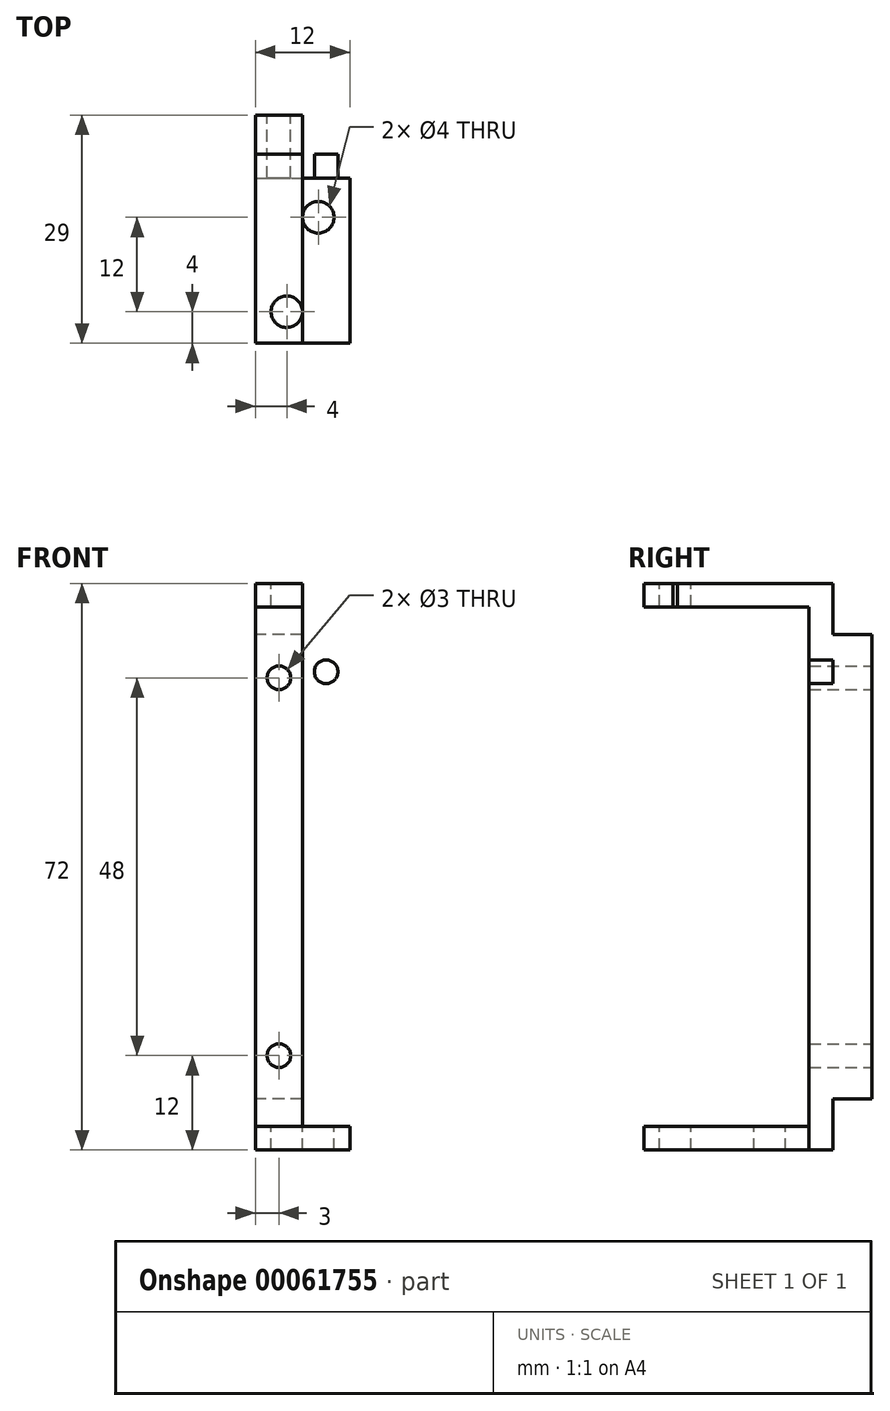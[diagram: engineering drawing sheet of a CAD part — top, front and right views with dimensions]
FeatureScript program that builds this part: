
annotation { "Feature Type Name" : "Feature", "Feature Type Description" : "" }
export const myFeature = defineFeature(function(context is Context, id is Id, definition is map)
    precondition{}
    {
        {
            var Q0;
            Q0=qCreatedBy(makeId("Right.planeOp"),FACE);
            var sketch = newSketch(context, id + "F0", { "sketchPlane" : qUnion([Q0])});
            skLineSegment(sketch, "E0", {"start": v(-10.5, 37.5) * mm, "end": v(18.5, 37.5) * mm});
            skLineSegment(sketch, "E1", {"start": v(18.5, 37.5) * mm, "end": v(18.5, -34.5) * mm});
            skLineSegment(sketch, "E2.0", {"start": v(10.5, 34.5) * mm, "end": v(10.5, -34.5) * mm});
            skLineSegment(sketch, "E2.1", {"start": v(-10.5, 34.5) * mm, "end": v(10.5, 34.5) * mm});
            skLineSegment(sketch, "E3", {"start": v(-10.5, 37.5) * mm, "end": v(-10.5, 34.5) * mm});
            skLineSegment(sketch, "E4", {"start": v(18.5, -34.5) * mm, "end": v(10.5, -34.5) * mm});
            skLineSegment(sketch, "E5", {"start": v(10.5, 0) * mm, "end": v(-14.36, 0) * mm, "construction": true});
            skLineSegment(sketch, "E6", {"start": v(0, 34.5) * mm, "end": v(0, -1.72) * mm, "construction": true});
            skSolve(sketch);
        }
        {
            var Q0;
            Q0=makeQuery(id+"F0.imprint","IMPRINT",FACE,{"disambiguationData":[TD([[makeQuery(id+"F0.imprint","IMPRINT",EDGE,{"derivedFrom":sQuery(id+"F0.wireOp",EDGE,"E0")}),-1.0]])]});
            extrude(context, id + "F1", {"entities" : qUnion([Q0]), "depth" : 12 * mm});
        }
        {
            var Q0;
            Q0=makeQuery(id+"F1.opExtrude","SWEPT_FACE",FACE,{"disambiguationData":[OSD([sQuery(id+"F0.wireOp",EDGE,"E0")])]});
            var sketch = newSketch(context, id + "F2", { "sketchPlane" : qUnion([Q0])});
            skLineSegment(sketch, "E7.bottom", {"start": v(0, 18.5) * mm, "end": v(6.02, 18.5) * mm});
            skLineSegment(sketch, "E7.top", {"start": v(0, 13.5) * mm, "end": v(6.02, 13.5) * mm});
            skLineSegment(sketch, "E7.left", {"start": v(0, 18.5) * mm, "end": v(0, 13.5) * mm});
            skLineSegment(sketch, "E7.right", {"start": v(6.02, 18.5) * mm, "end": v(6.02, 13.5) * mm});
            skSolve(sketch);
        }
        {
            var Q0;
            Q0=makeQuery(id+"F2.imprint","IMPRINT",FACE,{"disambiguationData":[TD([[makeQuery(id+"F2.imprint","IMPRINT",EDGE,{"derivedFrom":sQuery(id+"F2.wireOp",EDGE,"E7.bottom")}),1.0]])]});
            extrude(context, id + "F3", {"entities" : qUnion([Q0]), "operationType" : NewBodyOperationType.REMOVE, "oppositeDirection" : true, "depth" : 72 * mm});
        }
        {
            var Q0;
            Q0=makeQuery(id+"F1.opExtrude","SWEPT_FACE",FACE,{"disambiguationData":[OSD([sQuery(id+"F0.wireOp",EDGE,"E1")])]});
            var sketch = newSketch(context, id + "F4", { "sketchPlane" : qUnion([Q0])});
            skCircle(sketch, "E8", {"center": v(-9, 25.5) * mm, "radius": 1.5 * mm});
            skCircle(sketch, "E9", {"center": v(-9, -22.5) * mm, "radius": 1.5 * mm});
            skLineSegment(sketch, "E10", {"start": v(-9, 25.5) * mm, "end": v(-9, -22.5) * mm, "construction": true});
            skPoint(sketch, "E11", {"position": v(-9, 37.5) * mm});
            skLineSegment(sketch, "E12", {"start": v(-9, 25.5) * mm, "end": v(-9, 37.5) * mm, "construction": true});
            skSolve(sketch);
        }
        {
            var Q0;
            Q0=makeQuery(id+"F4.imprint","IMPRINT",FACE,{"disambiguationData":[TD([[makeQuery(id+"F4.imprint","IMPRINT",EDGE,{"derivedFrom":sQuery(id+"F4.wireOp",EDGE,"E8")}),1.0]])]});
            var Q1;
            Q1=makeQuery(id+"F4.imprint","IMPRINT",FACE,{"disambiguationData":[TD([[makeQuery(id+"F4.imprint","IMPRINT",EDGE,{"derivedFrom":sQuery(id+"F4.wireOp",EDGE,"E9")}),1.0]])]});
            extrude(context, id + "F5", {"entities" : qUnion([Q0, Q1]), "operationType" : NewBodyOperationType.REMOVE, "oppositeDirection" : true, "depth" : 25 * mm});
        }
        {
            var Q0;
            Q0=makeQuery(id+"F3.boolean.opBoolean","COPY",FACE,{"derivedFrom":makeQuery(id+"F3.opExtrude","SWEPT_FACE",FACE,{"disambiguationData":[OSD([sQuery(id+"F2.wireOp",EDGE,"E7.top")])]})});
            var sketch = newSketch(context, id + "F6", { "sketchPlane" : qUnion([Q0])});
            skCircle(sketch, "E13.0", {"center": v(-3, 26.27) * mm, "radius": 1.5 * mm});
            skCircle(sketch, "E14.0", {"center": v(-3, -23.27) * mm, "radius": 1.5 * mm});
            skLineSegment(sketch, "E15", {"start": v(-3, 37.5) * mm, "end": v(-3, 26.27) * mm, "construction": true});
            skLineSegment(sketch, "E16", {"start": v(-3, 26.27) * mm, "end": v(-3, -23.27) * mm, "construction": true});
            skSolve(sketch);
        }
        {
            var Q0;
            Q0=makeQuery(id+"F6.imprint","IMPRINT",FACE,{"disambiguationData":[TD([[makeQuery(id+"F6.imprint","IMPRINT",EDGE,{"derivedFrom":sQuery(id+"F6.wireOp",EDGE,"E14.0")}),1.0]])]});
            var Q1;
            Q1=makeQuery(id+"F6.imprint","IMPRINT",FACE,{"disambiguationData":[TD([[makeQuery(id+"F6.imprint","IMPRINT",EDGE,{"derivedFrom":sQuery(id+"F6.wireOp",EDGE,"E13.0")}),-1.0]])]});
            extrude(context, id + "F7", {"entities" : qUnion([Q0, Q1]), "operationType" : NewBodyOperationType.REMOVE, "oppositeDirection" : true, "depth" : 25 * mm});
        }
        {
            var Q0;
            Q0=makeQuery(id+"F1.opExtrude","SWEPT_FACE",FACE,{"disambiguationData":[OSD([sQuery(id+"F0.wireOp",EDGE,"E2.0")])]});
            var sketch = newSketch(context, id + "F8", { "sketchPlane" : qUnion([Q0])});
            skLineSegment(sketch, "E17.bottom", {"start": v(12, -34.5) * mm, "end": v(0, -34.5) * mm});
            skLineSegment(sketch, "E17.top", {"start": v(12, -31.5) * mm, "end": v(0, -31.5) * mm});
            skLineSegment(sketch, "E17.left", {"start": v(12, -34.5) * mm, "end": v(12, -31.5) * mm});
            skLineSegment(sketch, "E17.right", {"start": v(0, -34.5) * mm, "end": v(0, -31.5) * mm});
            skSolve(sketch);
        }
        {
            var Q0;
            Q0=makeQuery(id+"F8.imprint","IMPRINT",FACE,{"disambiguationData":[TD([[makeQuery(id+"F8.imprint","IMPRINT",EDGE,{"derivedFrom":sQuery(id+"F8.wireOp",EDGE,"E17.bottom")}),-1.0]])]});
            extrude(context, id + "F9", {"entities" : qUnion([Q0]), "operationType" : NewBodyOperationType.ADD, "depth" : 21 * mm});
        }
        {
            var Q0;
            Q0=makeQuery(id+"F1.opExtrude","SWEPT_FACE",FACE,{"disambiguationData":[OSD([sQuery(id+"F0.wireOp",EDGE,"E0")])]});
            var sketch = newSketch(context, id + "F10", { "sketchPlane" : qUnion([Q0])});
            skCircle(sketch, "E18", {"center": v(4, 5.5) * mm, "radius": 2 * mm});
            skCircle(sketch, "E19", {"center": v(8, -6.5) * mm, "radius": 2 * mm});
            skSolve(sketch);
        }
        {
            var Q0;
            Q0=makeQuery(id+"F10.imprint","IMPRINT",FACE,{"disambiguationData":[TD([[makeQuery(id+"F10.imprint","IMPRINT",EDGE,{"derivedFrom":sQuery(id+"F10.wireOp",EDGE,"E18")}),1.0]])]});
            var Q1;
            Q1=makeQuery(id+"F10.imprint","IMPRINT",FACE,{"disambiguationData":[TD([[makeQuery(id+"F10.imprint","IMPRINT",EDGE,{"derivedFrom":sQuery(id+"F10.wireOp",EDGE,"E19")}),1.0]])]});
            extrude(context, id + "F11", {"entities" : qUnion([Q0, Q1]), "operationType" : NewBodyOperationType.REMOVE, "oppositeDirection" : true, "depth" : 72 * mm});
        }
        {
            var Q0;
            Q0=makeQuery(id+"F1.opExtrude","SWEPT_BODY",BODY,{"disambiguationData":[OSD([sQuery(id+"F0.wireOp",EDGE,"E0"),sQuery(id+"F0.wireOp",EDGE,"E1"),sQuery(id+"F0.wireOp",EDGE,"E2.0"),sQuery(id+"F0.wireOp",EDGE,"E2.1"),sQuery(id+"F0.wireOp",EDGE,"E3"),sQuery(id+"F0.wireOp",EDGE,"E4")])]});
            var Q1;
            Q1=makeQuery(id+"F1.opExtrude","CAP_FACE",FACE,{"disambiguationData":[OSD([sQuery(id+"F0.wireOp",EDGE,"E0"),sQuery(id+"F0.wireOp",EDGE,"E1"),sQuery(id+"F0.wireOp",EDGE,"E2.0"),sQuery(id+"F0.wireOp",EDGE,"E2.1"),sQuery(id+"F0.wireOp",EDGE,"E3"),sQuery(id+"F0.wireOp",EDGE,"E4")])],"isStart":false});
            mirror(context, id + "F12", {"entities" : qUnion([Q0]), "mirrorPlane" : qUnion([Q1])});
        }
        {
            var Q0;
            Q0=makeQuery(id+"F1.opExtrude","SWEPT_BODY",BODY,{"disambiguationData":[OSD([sQuery(id+"F0.wireOp",EDGE,"E0"),sQuery(id+"F0.wireOp",EDGE,"E1"),sQuery(id+"F0.wireOp",EDGE,"E2.0"),sQuery(id+"F0.wireOp",EDGE,"E2.1"),sQuery(id+"F0.wireOp",EDGE,"E3"),sQuery(id+"F0.wireOp",EDGE,"E4")])]});
            deleteBodies(context, id + "F13", {"entities" : qUnion([Q0])});
        }
        {
            var Q0;
            Q0=makeQuery(id+"F12.opPattern","COPY",FACE,{"derivedFrom":makeQuery(id+"F1.opExtrude","SWEPT_FACE",FACE,{"disambiguationData":[OSD([sQuery(id+"F0.wireOp",EDGE,"E1")])]}),"instanceName":"1"});
            var sketch = newSketch(context, id + "F14", { "sketchPlane" : qUnion([Q0])});
            skLineSegment(sketch, "E20.bottom", {"start": v(-17.98, 37.5) * mm, "end": v(-12, 37.5) * mm});
            skLineSegment(sketch, "E20.top", {"start": v(-17.98, 31) * mm, "end": v(-12, 31) * mm});
            skLineSegment(sketch, "E20.left", {"start": v(-17.98, 37.5) * mm, "end": v(-17.98, 31) * mm});
            skLineSegment(sketch, "E20.right", {"start": v(-12, 37.5) * mm, "end": v(-12, 31) * mm});
            skLineSegment(sketch, "E21.bottom", {"start": v(-17.98, -34.5) * mm, "end": v(-12, -34.5) * mm});
            skLineSegment(sketch, "E21.top", {"start": v(-17.98, -28) * mm, "end": v(-12, -28) * mm});
            skLineSegment(sketch, "E21.left", {"start": v(-17.98, -34.5) * mm, "end": v(-17.98, -28) * mm});
            skLineSegment(sketch, "E21.right", {"start": v(-12, -34.5) * mm, "end": v(-12, -28) * mm});
            skSolve(sketch);
        }
        {
            var Q0;
            Q0 = qSketchRegion(id + "F14", true);
            extrude(context, id + "F15", {"entities" : qUnion([Q0]), "operationType" : NewBodyOperationType.REMOVE, "oppositeDirection" : true, "depth" : 5 * mm});
        }
    });
